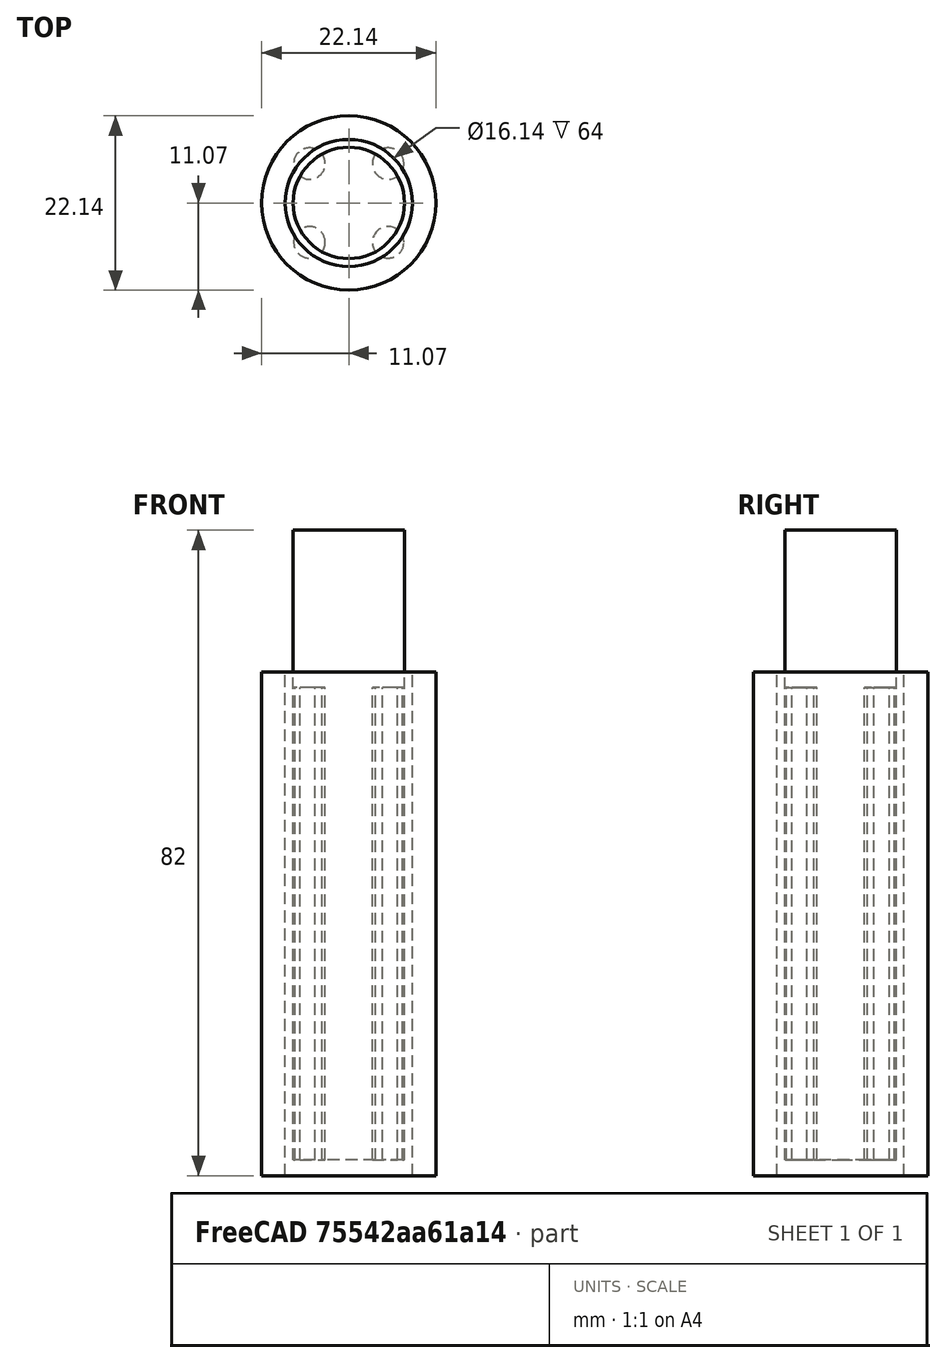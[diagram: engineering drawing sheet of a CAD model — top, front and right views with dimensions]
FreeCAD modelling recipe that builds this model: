
FCSTD DOCUMENT  (FreeCAD 0.14R3692 (Git))
Label: actuator2
License: CC-BY 3.0
LicenseURL: http://creativecommons.org/licenses/by/3.0/
objects: Part::Cylinder×11, Part::Cut×9
note: 20 computed .brp shape members not serialized (recipe doc carries the construction recipe); baked Part::Feature solids carry a one-line shape summary decoded from their .brp

FEATURE [Part::Cylinder] Cylinder
  Angle = 360
  Height = 60
  Radius = 2
FEATURE [Part::Cylinder] Cylinder001
  Angle = 360
  Height = 60
  Placement = pos=(0,10,0) rot=(0,0,1;0rad)
  Radius = 2
FEATURE [Part::Cylinder] Cylinder002
  Angle = 360
  Height = 60
  Placement = pos=(10,0,0) rot=(0,0,1;0rad)
  Radius = 2
FEATURE [Part::Cylinder] Cylinder003
  Angle = 360
  Height = 60
  Placement = pos=(10,10,0) rot=(0,0,1;0rad)
  Radius = 2
FEATURE [Part::Cylinder] Cylinder004
  Angle = 360
  Height = 80
  Placement = pos=(5,5,0) rot=(0,0,1;0rad)
  Radius = 7.071
FEATURE [Part::Cut] Cut
  Base = -> Cylinder004
  Tool = -> Cylinder003
FEATURE [Part::Cut] Cut001
  Base = -> Cut
  Tool = -> Cylinder002
FEATURE [Part::Cut] Cut002
  Base = -> Cut001
  Tool = -> Cylinder001
FEATURE [Part::Cut] Cut003
  Base = -> Cut002
  Tool = -> Cylinder
FEATURE [Part::Cylinder] Cylinder005
  Angle = 360
  Height = 60
  Radius = 2
FEATURE [Part::Cylinder] Cylinder006
  Angle = 360
  Height = 60
  Placement = pos=(0,10,0) rot=(0,0,1;0rad)
  Radius = 2
FEATURE [Part::Cylinder] Cylinder007
  Angle = 360
  Height = 60
  Placement = pos=(10,0,0) rot=(0,0,1;0rad)
  Radius = 2
FEATURE [Part::Cylinder] Cylinder008
  Angle = 360
  Height = 60
  Placement = pos=(10,10,0) rot=(0,0,1;0rad)
  Radius = 2
FEATURE [Part::Cylinder] Cylinder009
  Angle = 360
  Height = 64
  Placement = pos=(5,5,-2) rot=(0,0,1;0rad)
  Radius = 11.071
FEATURE [Part::Cylinder] Cylinder010
  Angle = 360
  Height = 80
  Placement = pos=(5,5,-3) rot=(0,0,1;0rad)
  Radius = 8.071
FEATURE [Part::Cut] Cut004
  Base = -> Cylinder009
  Tool = -> Cylinder010
FEATURE [Part::Cut] Cut005
  Base = -> Cut004
  Tool = -> Cylinder008
FEATURE [Part::Cut] Cut006
  Base = -> Cut005
  Tool = -> Cylinder007
FEATURE [Part::Cut] Cut007
  Base = -> Cut006
  Tool = -> Cylinder006
FEATURE [Part::Cut] Cut008
  Base = -> Cut007
  Tool = -> Cylinder005
